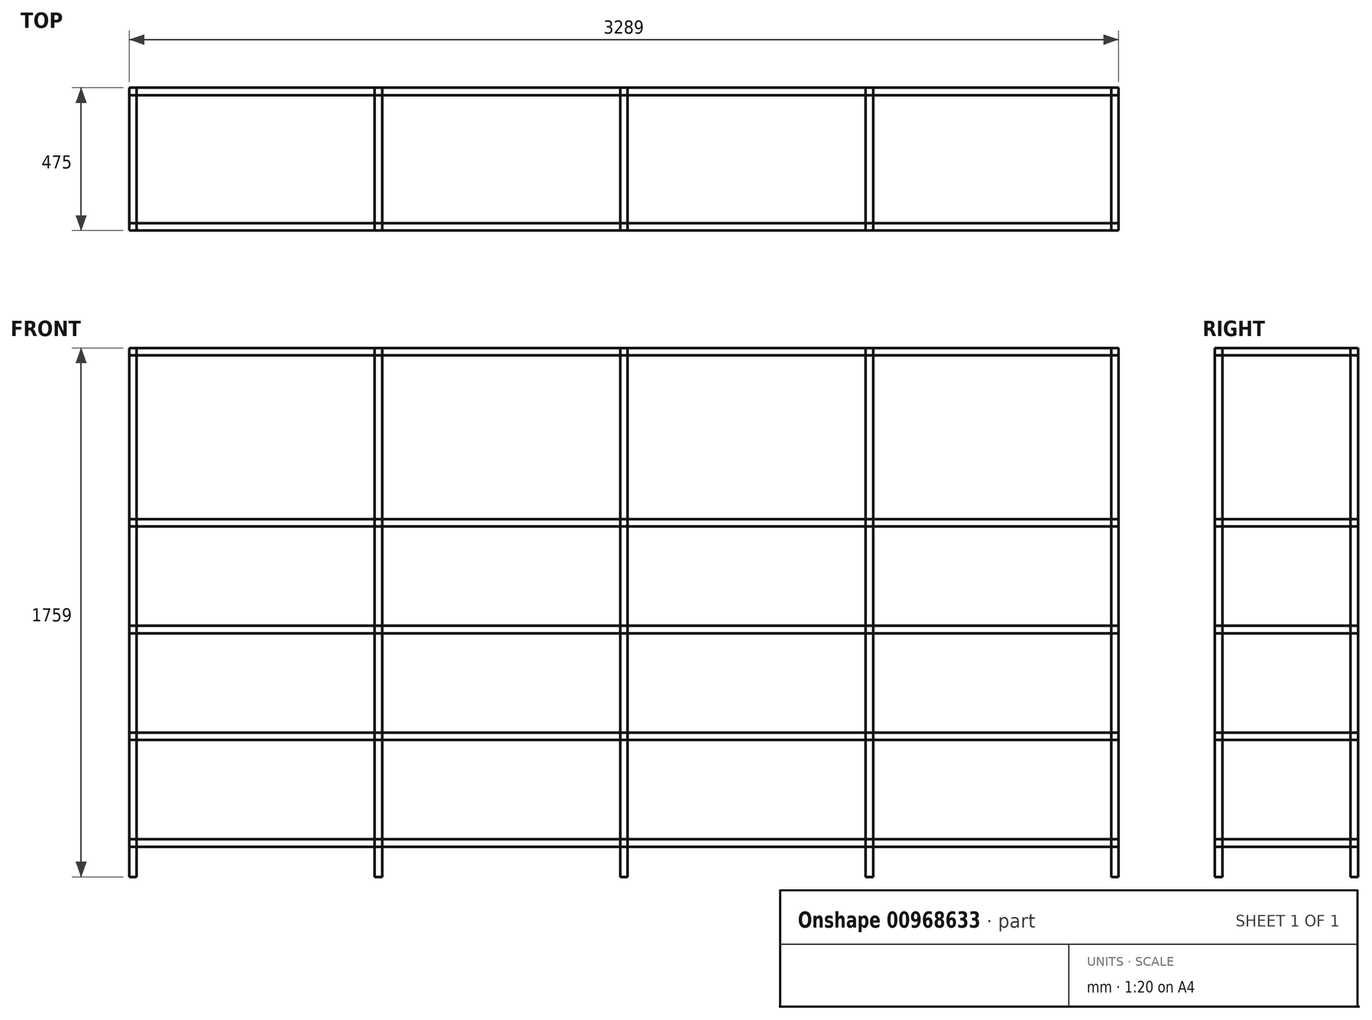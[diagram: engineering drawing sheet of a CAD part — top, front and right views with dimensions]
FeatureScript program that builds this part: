
annotation { "Feature Type Name" : "Feature", "Feature Type Description" : "" }
export const myFeature = defineFeature(function(context is Context, id is Id, definition is map)
    precondition{}
    {
        {
            var Q0;
            Q0=qCreatedBy(makeId("Top.planeOp"),FACE);
            var sketch = newSketch(context, id + "F0", { "sketchPlane" : qUnion([Q0])});
            skLineSegment(sketch, "E0.bottom", {"start": v(-20.38, 8.23) * mm, "end": v(4.62, 8.23) * mm});
            skLineSegment(sketch, "E0.top", {"start": v(-20.38, -16.77) * mm, "end": v(4.62, -16.77) * mm});
            skLineSegment(sketch, "E0.left", {"start": v(-20.38, 8.23) * mm, "end": v(-20.38, -16.77) * mm});
            skLineSegment(sketch, "E0.right", {"start": v(4.62, 8.23) * mm, "end": v(4.62, -16.77) * mm});
            skSolve(sketch);
        }
        {
            var Q0;
            Q0 = qSketchRegion(id + "F0", true);
            extrude(context, id + "F1", {"entities" : qUnion([Q0]), "depth" : 25 * mm, "offsetDistance" : 25 * mm});
        }
        {
            var Q0;
            Q0=makeQuery(id+"F1.opExtrude","SWEPT_FACE",FACE,{"disambiguationData":[OSD([sQuery(id+"F0.wireOp",EDGE,"E0.right")])]});
            extrude(context, id + "F2", {"entities" : qUnion([Q0]), "depth" : 791 * mm, "offsetDistance" : 25 * mm, "hasSecondDirection" : true, "secondDirectionOppositeDirection" : true, "secondDirectionDepth" : 0 * mm});
        }
        {
            var Q0;
            Q0=makeQuery(id+"F2.opExtrude","CAP_FACE",FACE,{"disambiguationData":[OSD([sQuery(id+"F0.wireOp",EDGE,"E0.right")])],"isStart":false});
            extrude(context, id + "F3", {"entities" : qUnion([Q0]), "depth" : 25 * mm, "offsetDistance" : 25 * mm, "hasSecondDirection" : true, "secondDirectionOppositeDirection" : true, "secondDirectionDepth" : 0 * mm});
        }
        {
            var Q0;
            Q0=makeQuery(id+"F3.opExtrude","SWEPT_FACE",FACE,{"disambiguationData":[OSD([sQuery(id+"F0.wireOp",EDGE,"E0.top"),sQuery(id+"F0.wireOp",EDGE,"E0.right")])]});
            var Q1;
            Q1=makeQuery(id+"F1.opExtrude","SWEPT_FACE",FACE,{"disambiguationData":[OSD([sQuery(id+"F0.wireOp",EDGE,"E0.top")])]});
            extrude(context, id + "F4", {"entities" : qUnion([Q0, Q1]), "depth" : 425 * mm, "offsetDistance" : 25 * mm, "hasSecondDirection" : true, "secondDirectionOppositeDirection" : true, "secondDirectionDepth" : 0 * mm});
        }
        {
            var Q0;
            Q0=makeQuery(id+"F4.opExtrude","CAP_FACE",FACE,{"disambiguationData":[OSD([sQuery(id+"F0.wireOp",EDGE,"E0.top")])],"isStart":false});
            var Q1;
            Q1=makeQuery(id+"F4.opExtrude","CAP_FACE",FACE,{"disambiguationData":[OSD([sQuery(id+"F0.wireOp",EDGE,"E0.top"),sQuery(id+"F0.wireOp",EDGE,"E0.right")])],"isStart":false});
            extrude(context, id + "F5", {"entities" : qUnion([Q0, Q1]), "depth" : 25 * mm, "offsetDistance" : 25 * mm, "hasSecondDirection" : true, "secondDirectionOppositeDirection" : true, "secondDirectionDepth" : 0 * mm});
        }
        {
            var Q0;
            {var subQ0=sQuery(id+"F0.wireOp",EDGE,"E0.right");var subQ1=sQuery(id+"F0.wireOp",EDGE,"E0.top");Q0=makeQuery(id+"F5.opExtrude","SWEPT_FACE",FACE,{"disambiguationData":[OSD([subQ1,subQ0]),TDD([makeQuery(id+"F4.opExtrude","CAP_EDGE",EDGE,{"disambiguationData":[OSD([subQ1,subQ0]),TDD([makeQuery(id+"F1.opExtrude","SWEPT_EDGE",EDGE,{"disambiguationData":[OSD([subQ1,subQ0])]})])],"isStart":false})])]});}
            extrude(context, id + "F6", {"entities" : qUnion([Q0]), "depth" : 791 * mm, "offsetDistance" : 25 * mm, "hasSecondDirection" : true, "secondDirectionOppositeDirection" : true, "secondDirectionDepth" : 0 * mm});
        }
        {
            var Q0;
            {var subQ0=sQuery(id+"F0.wireOp",EDGE,"E0.top");Q0=makeQuery(id+"F5.opExtrude","SWEPT_FACE",FACE,{"disambiguationData":[OSD([subQ0]),TDD([makeQuery(id+"F4.opExtrude","CAP_EDGE",EDGE,{"disambiguationData":[OSD([subQ0]),TDD([makeQuery(id+"F1.opExtrude","CAP_EDGE",EDGE,{"disambiguationData":[OSD([subQ0])],"isStart":false})])],"isStart":false})])]});}
            var Q1;
            Q1=makeQuery(id+"F1.opExtrude","CAP_FACE",FACE,{"disambiguationData":[OSD([sQuery(id+"F0.wireOp",EDGE,"E0.bottom"),sQuery(id+"F0.wireOp",EDGE,"E0.top"),sQuery(id+"F0.wireOp",EDGE,"E0.left"),sQuery(id+"F0.wireOp",EDGE,"E0.right")])],"isStart":false});
            var Q2;
            {var subQ0=sQuery(id+"F0.wireOp",EDGE,"E0.right");Q2=makeQuery(id+"F3.opExtrude","SWEPT_FACE",FACE,{"disambiguationData":[OSD([subQ0]),TDD([makeQuery(id+"F2.opExtrude","CAP_EDGE",EDGE,{"disambiguationData":[OSD([subQ0]),TDD([makeQuery(id+"F1.opExtrude","CAP_EDGE",EDGE,{"disambiguationData":[OSD([subQ0])],"isStart":false})])],"isStart":false})])]});}
            var Q3;
            {var subQ0=sQuery(id+"F0.wireOp",EDGE,"E0.right");var subQ1=sQuery(id+"F0.wireOp",EDGE,"E0.top");Q3=makeQuery(id+"F5.opExtrude","SWEPT_FACE",FACE,{"disambiguationData":[OSD([subQ1,subQ0]),TDD([makeQuery(id+"F4.opExtrude","CAP_EDGE",EDGE,{"disambiguationData":[OSD([subQ1,subQ0]),TDD([makeQuery(id+"F3.opExtrude","SWEPT_EDGE",EDGE,{"disambiguationData":[OSD([subQ1,subQ0]),TDD([makeQuery(id+"F2.opExtrude","CAP_VERTEX",VERTEX,{"disambiguationData":[OSD([subQ1,subQ0]),TDD([makeQuery(id+"F1.opExtrude","CAP_VERTEX",VERTEX,{"disambiguationData":[OSD([subQ1,subQ0])],"isStart":false})])],"isStart":false})])]})])],"isStart":false})])]});}
            extrude(context, id + "F7", {"entities" : qUnion([Q0, Q1, Q2, Q3]), "depth" : 544 * mm, "offsetDistance" : 25 * mm, "hasSecondDirection" : true, "secondDirectionOppositeDirection" : true, "secondDirectionDepth" : 0 * mm});
        }
        {
            var Q0;
            Q0=makeQuery(id+"F7.opExtrude","CAP_FACE",FACE,{"disambiguationData":[OSD([sQuery(id+"F0.wireOp",EDGE,"E0.bottom"),sQuery(id+"F0.wireOp",EDGE,"E0.top"),sQuery(id+"F0.wireOp",EDGE,"E0.left"),sQuery(id+"F0.wireOp",EDGE,"E0.right")])],"isStart":false});
            var Q1;
            Q1=makeQuery(id+"F7.opExtrude","CAP_FACE",FACE,{"disambiguationData":[OSD([sQuery(id+"F0.wireOp",EDGE,"E0.top")])],"isStart":false});
            var Q2;
            Q2=makeQuery(id+"F7.opExtrude","CAP_FACE",FACE,{"disambiguationData":[OSD([sQuery(id+"F0.wireOp",EDGE,"E0.top"),sQuery(id+"F0.wireOp",EDGE,"E0.right")])],"isStart":false});
            var Q3;
            Q3=makeQuery(id+"F7.opExtrude","CAP_FACE",FACE,{"disambiguationData":[OSD([sQuery(id+"F0.wireOp",EDGE,"E0.right")])],"isStart":false});
            extrude(context, id + "F8", {"entities" : qUnion([Q0, Q1, Q2, Q3]), "depth" : 25 * mm, "offsetDistance" : 25 * mm, "hasSecondDirection" : true, "secondDirectionOppositeDirection" : true, "secondDirectionDepth" : 0 * mm});
        }
        {
            var Q0;
            {var subQ0=sQuery(id+"F0.wireOp",EDGE,"E0.right");Q0=makeQuery(id+"F8.opExtrude","SWEPT_FACE",FACE,{"disambiguationData":[OSD([subQ0]),TDD([makeQuery(id+"F7.opExtrude","CAP_EDGE",EDGE,{"disambiguationData":[OSD([subQ0]),TDD([makeQuery(id+"F1.opExtrude","CAP_EDGE",EDGE,{"disambiguationData":[OSD([subQ0])],"isStart":false})])],"isStart":false})])]});}
            var Q1;
            {var subQ0=sQuery(id+"F0.wireOp",EDGE,"E0.right");var subQ1=sQuery(id+"F0.wireOp",EDGE,"E0.top");Q1=makeQuery(id+"F8.opExtrude","SWEPT_FACE",FACE,{"disambiguationData":[OSD([subQ1,subQ0]),TDD([makeQuery(id+"F7.opExtrude","CAP_EDGE",EDGE,{"disambiguationData":[OSD([subQ1,subQ0]),TDD([makeQuery(id+"F5.opExtrude","SWEPT_EDGE",EDGE,{"disambiguationData":[OSD([subQ1,subQ0]),TDD([makeQuery(id+"F4.opExtrude","CAP_VERTEX",VERTEX,{"disambiguationData":[OSD([subQ1,subQ0]),TDD([makeQuery(id+"F1.opExtrude","CAP_VERTEX",VERTEX,{"disambiguationData":[OSD([subQ1,subQ0])],"isStart":false})])],"isStart":false})])]})])],"isStart":false})])]});}
            extrude(context, id + "F9", {"entities" : qUnion([Q0, Q1]), "depth" : 791 * mm, "offsetDistance" : 25 * mm, "hasSecondDirection" : true, "secondDirectionOppositeDirection" : true, "secondDirectionDepth" : 0 * mm});
        }
        {
            var Q0;
            {var subQ0=sQuery(id+"F0.wireOp",EDGE,"E0.right");var subQ1=sQuery(id+"F0.wireOp",EDGE,"E0.top");Q0=makeQuery(id+"F8.opExtrude","SWEPT_FACE",FACE,{"disambiguationData":[OSD([subQ1,subQ0]),TDD([makeQuery(id+"F7.opExtrude","CAP_EDGE",EDGE,{"disambiguationData":[OSD([subQ1,subQ0]),TDD([makeQuery(id+"F5.opExtrude","CAP_EDGE",EDGE,{"disambiguationData":[OSD([subQ1,subQ0]),TDD([makeQuery(id+"F4.opExtrude","CAP_EDGE",EDGE,{"disambiguationData":[OSD([subQ1,subQ0]),TDD([makeQuery(id+"F3.opExtrude","SWEPT_EDGE",EDGE,{"disambiguationData":[OSD([subQ1,subQ0]),TDD([makeQuery(id+"F2.opExtrude","CAP_VERTEX",VERTEX,{"disambiguationData":[OSD([subQ1,subQ0]),TDD([makeQuery(id+"F1.opExtrude","CAP_VERTEX",VERTEX,{"disambiguationData":[OSD([subQ1,subQ0])],"isStart":false})])],"isStart":false})])]})])],"isStart":false})])],"isStart":true})])],"isStart":false})])]});}
            extrude(context, id + "F10", {"entities" : qUnion([Q0]), "depth" : 425 * mm, "offsetDistance" : 25 * mm});
        }
        {
            var Q0;
            {var subQ0=sQuery(id+"F0.wireOp",EDGE,"E0.top");Q0=makeQuery(id+"F8.opExtrude","SWEPT_FACE",FACE,{"disambiguationData":[OSD([subQ0]),TDD([makeQuery(id+"F7.opExtrude","CAP_EDGE",EDGE,{"disambiguationData":[OSD([subQ0]),TDD([makeQuery(id+"F5.opExtrude","CAP_EDGE",EDGE,{"disambiguationData":[OSD([subQ0]),TDD([makeQuery(id+"F4.opExtrude","CAP_EDGE",EDGE,{"disambiguationData":[OSD([subQ0]),TDD([makeQuery(id+"F1.opExtrude","CAP_EDGE",EDGE,{"disambiguationData":[OSD([subQ0])],"isStart":false})])],"isStart":false})])],"isStart":true})])],"isStart":false})])]});}
            extrude(context, id + "F11", {"entities" : qUnion([Q0]), "depth" : 425 * mm, "offsetDistance" : 25 * mm, "hasSecondDirection" : true, "secondDirectionOppositeDirection" : true, "secondDirectionDepth" : 0 * mm});
        }
        {
            var Q0;
            {var subQ0=sQuery(id+"F0.wireOp",EDGE,"E0.right");var subQ1=sQuery(id+"F0.wireOp",EDGE,"E0.top");Q0=makeQuery(id+"F5.opExtrude","SWEPT_FACE",FACE,{"disambiguationData":[OSD([subQ1,subQ0]),TDD([makeQuery(id+"F4.opExtrude","CAP_EDGE",EDGE,{"disambiguationData":[OSD([subQ1,subQ0]),TDD([makeQuery(id+"F3.opExtrude","SWEPT_EDGE",EDGE,{"disambiguationData":[OSD([subQ1,subQ0]),TDD([makeQuery(id+"F2.opExtrude","CAP_VERTEX",VERTEX,{"disambiguationData":[OSD([subQ1,subQ0]),TDD([makeQuery(id+"F1.opExtrude","CAP_VERTEX",VERTEX,{"disambiguationData":[OSD([subQ1,subQ0])],"isStart":true})])],"isStart":false})])]})])],"isStart":false})])]});}
            var Q1;
            {var subQ0=sQuery(id+"F0.wireOp",EDGE,"E0.right");Q1=makeQuery(id+"F3.opExtrude","SWEPT_FACE",FACE,{"disambiguationData":[OSD([subQ0]),TDD([makeQuery(id+"F2.opExtrude","CAP_EDGE",EDGE,{"disambiguationData":[OSD([subQ0]),TDD([makeQuery(id+"F1.opExtrude","CAP_EDGE",EDGE,{"disambiguationData":[OSD([subQ0])],"isStart":true})])],"isStart":false})])]});}
            var Q2;
            {var subQ0=sQuery(id+"F0.wireOp",EDGE,"E0.top");Q2=makeQuery(id+"F5.opExtrude","SWEPT_FACE",FACE,{"disambiguationData":[OSD([subQ0]),TDD([makeQuery(id+"F4.opExtrude","CAP_EDGE",EDGE,{"disambiguationData":[OSD([subQ0]),TDD([makeQuery(id+"F1.opExtrude","CAP_EDGE",EDGE,{"disambiguationData":[OSD([subQ0])],"isStart":true})])],"isStart":false})])]});}
            var Q3;
            Q3=makeQuery(id+"F1.opExtrude","CAP_FACE",FACE,{"disambiguationData":[OSD([sQuery(id+"F0.wireOp",EDGE,"E0.bottom"),sQuery(id+"F0.wireOp",EDGE,"E0.top"),sQuery(id+"F0.wireOp",EDGE,"E0.left"),sQuery(id+"F0.wireOp",EDGE,"E0.right")])],"isStart":true});
            extrude(context, id + "F12", {"entities" : qUnion([Q0, Q1, Q2, Q3]), "depth" : 330 * mm, "offsetDistance" : 25 * mm, "hasSecondDirection" : true, "secondDirectionOppositeDirection" : true, "secondDirectionDepth" : 0 * mm});
        }
        {
            var Q0;
            Q0=makeQuery(id+"F12.opExtrude","CAP_FACE",FACE,{"disambiguationData":[OSD([sQuery(id+"F0.wireOp",EDGE,"E0.top")])],"isStart":false});
            extrude(context, id + "F13", {"entities" : qUnion([Q0]), "depth" : 25 * mm, "offsetDistance" : 25 * mm, "hasSecondDirection" : true, "secondDirectionOppositeDirection" : true, "secondDirectionDepth" : 0 * mm});
        }
        {
            var Q0;
            Q0=makeQuery(id+"F13.opExtrude","CAP_FACE",FACE,{"disambiguationData":[OSD([sQuery(id+"F0.wireOp",EDGE,"E0.top")])],"isStart":false});
            extrude(context, id + "F14", {"entities" : qUnion([Q0]), "depth" : 330 * mm, "offsetDistance" : 25 * mm, "hasSecondDirection" : true, "secondDirectionOppositeDirection" : true, "secondDirectionDepth" : 0 * mm});
        }
        {
            var Q0;
            Q0=makeQuery(id+"F14.opExtrude","CAP_FACE",FACE,{"disambiguationData":[OSD([sQuery(id+"F0.wireOp",EDGE,"E0.top")])],"isStart":false});
            extrude(context, id + "F15", {"entities" : qUnion([Q0]), "depth" : 25 * mm, "offsetDistance" : 25 * mm, "hasSecondDirection" : true, "secondDirectionOppositeDirection" : true, "secondDirectionDepth" : 0 * mm});
        }
        {
            var Q0;
            Q0=makeQuery(id+"F15.opExtrude","CAP_FACE",FACE,{"disambiguationData":[OSD([sQuery(id+"F0.wireOp",EDGE,"E0.top")])],"isStart":false});
            extrude(context, id + "F16", {"entities" : qUnion([Q0]), "depth" : 330 * mm, "offsetDistance" : 25 * mm, "hasSecondDirection" : true, "secondDirectionOppositeDirection" : true, "secondDirectionDepth" : 0 * mm});
        }
        {
            var Q0;
            Q0=makeQuery(id+"F16.opExtrude","CAP_FACE",FACE,{"disambiguationData":[OSD([sQuery(id+"F0.wireOp",EDGE,"E0.top")])],"isStart":false});
            extrude(context, id + "F17", {"entities" : qUnion([Q0]), "depth" : 25 * mm, "offsetDistance" : 25 * mm, "hasSecondDirection" : true, "secondDirectionOppositeDirection" : true, "secondDirectionDepth" : 0 * mm});
        }
        {
            var Q0;
            Q0=makeQuery(id+"F17.opExtrude","CAP_FACE",FACE,{"disambiguationData":[OSD([sQuery(id+"F0.wireOp",EDGE,"E0.top")])],"isStart":false});
            extrude(context, id + "F18", {"entities" : qUnion([Q0]), "depth" : 100 * mm, "offsetDistance" : 25 * mm, "hasSecondDirection" : true, "secondDirectionOppositeDirection" : true, "secondDirectionDepth" : 0 * mm});
        }
        {
            var Q0;
            Q0=makeQuery(id+"F12.opExtrude","SWEPT_BODY",BODY,{"disambiguationData":[OSD([sQuery(id+"F0.wireOp",EDGE,"E0.bottom"),sQuery(id+"F0.wireOp",EDGE,"E0.top"),sQuery(id+"F0.wireOp",EDGE,"E0.left"),sQuery(id+"F0.wireOp",EDGE,"E0.right")])]});
            deleteBodies(context, id + "F19", {"entities" : qUnion([Q0])});
        }
        {
            var Q0;
            Q0=makeQuery(id+"F12.opExtrude","SWEPT_BODY",BODY,{"disambiguationData":[OSD([sQuery(id+"F0.wireOp",EDGE,"E0.top"),sQuery(id+"F0.wireOp",EDGE,"E0.right")])]});
            deleteBodies(context, id + "F20", {"entities" : qUnion([Q0])});
        }
        {
            var Q0;
            Q0=makeQuery(id+"F12.opExtrude","SWEPT_BODY",BODY,{"disambiguationData":[OSD([sQuery(id+"F0.wireOp",EDGE,"E0.right")])]});
            deleteBodies(context, id + "F21", {"entities" : qUnion([Q0])});
        }
        {
            var Q0;
            Q0=makeQuery(id+"F12.opExtrude","SWEPT_BODY",BODY,{"disambiguationData":[OSD([sQuery(id+"F0.wireOp",EDGE,"E0.top")])]});
            var Q1;
            Q1=makeQuery(id+"F13.opExtrude","SWEPT_BODY",BODY,{"disambiguationData":[OSD([sQuery(id+"F0.wireOp",EDGE,"E0.top")])]});
            var Q2;
            Q2=makeQuery(id+"F14.opExtrude","SWEPT_BODY",BODY,{"disambiguationData":[OSD([sQuery(id+"F0.wireOp",EDGE,"E0.top")])]});
            var Q3;
            Q3=makeQuery(id+"F15.opExtrude","SWEPT_BODY",BODY,{"disambiguationData":[OSD([sQuery(id+"F0.wireOp",EDGE,"E0.top")])]});
            var Q4;
            Q4=makeQuery(id+"F16.opExtrude","SWEPT_BODY",BODY,{"disambiguationData":[OSD([sQuery(id+"F0.wireOp",EDGE,"E0.top")])]});
            var Q5;
            Q5=makeQuery(id+"F17.opExtrude","SWEPT_BODY",BODY,{"disambiguationData":[OSD([sQuery(id+"F0.wireOp",EDGE,"E0.top")])]});
            var Q6;
            Q6=makeQuery(id+"F18.opExtrude","SWEPT_BODY",BODY,{"disambiguationData":[OSD([sQuery(id+"F0.wireOp",EDGE,"E0.top")])]});
            transform(context, id + "F22", {"entities" : qUnion([Q0, Q1, Q2, Q3, Q4, Q5, Q6]), "transformType" : TransformType.TRANSLATION_3D, "dx" : 816 * mm, "dy" : 0 * mm, "dz" : 0 * mm, "makeCopy" : true});
        }
        {
            var Q0;
            Q0=makeQuery(id+"F22.opPattern","COPY",BODY,{"derivedFrom":makeQuery(id+"F12.opExtrude","SWEPT_BODY",BODY,{"disambiguationData":[OSD([sQuery(id+"F0.wireOp",EDGE,"E0.top")])]}),"instanceName":"1"});
            var Q1;
            Q1=makeQuery(id+"F22.opPattern","COPY",BODY,{"derivedFrom":makeQuery(id+"F13.opExtrude","SWEPT_BODY",BODY,{"disambiguationData":[OSD([sQuery(id+"F0.wireOp",EDGE,"E0.top")])]}),"instanceName":"1"});
            var Q2;
            Q2=makeQuery(id+"F22.opPattern","COPY",BODY,{"derivedFrom":makeQuery(id+"F14.opExtrude","SWEPT_BODY",BODY,{"disambiguationData":[OSD([sQuery(id+"F0.wireOp",EDGE,"E0.top")])]}),"instanceName":"1"});
            var Q3;
            Q3=makeQuery(id+"F22.opPattern","COPY",BODY,{"derivedFrom":makeQuery(id+"F18.opExtrude","SWEPT_BODY",BODY,{"disambiguationData":[OSD([sQuery(id+"F0.wireOp",EDGE,"E0.top")])]}),"instanceName":"1"});
            var Q4;
            Q4=makeQuery(id+"F22.opPattern","COPY",BODY,{"derivedFrom":makeQuery(id+"F16.opExtrude","SWEPT_BODY",BODY,{"disambiguationData":[OSD([sQuery(id+"F0.wireOp",EDGE,"E0.top")])]}),"instanceName":"1"});
            var Q5;
            Q5=makeQuery(id+"F22.opPattern","COPY",BODY,{"derivedFrom":makeQuery(id+"F17.opExtrude","SWEPT_BODY",BODY,{"disambiguationData":[OSD([sQuery(id+"F0.wireOp",EDGE,"E0.top")])]}),"instanceName":"1"});
            var Q6;
            Q6=makeQuery(id+"F22.opPattern","COPY",BODY,{"derivedFrom":makeQuery(id+"F15.opExtrude","SWEPT_BODY",BODY,{"disambiguationData":[OSD([sQuery(id+"F0.wireOp",EDGE,"E0.top")])]}),"instanceName":"1"});
            var Q7;
            Q7=makeQuery(id+"F18.opExtrude","SWEPT_BODY",BODY,{"disambiguationData":[OSD([sQuery(id+"F0.wireOp",EDGE,"E0.top")])]});
            var Q8;
            Q8=makeQuery(id+"F16.opExtrude","SWEPT_BODY",BODY,{"disambiguationData":[OSD([sQuery(id+"F0.wireOp",EDGE,"E0.top")])]});
            var Q9;
            Q9=makeQuery(id+"F12.opExtrude","SWEPT_BODY",BODY,{"disambiguationData":[OSD([sQuery(id+"F0.wireOp",EDGE,"E0.top")])]});
            var Q10;
            Q10=makeQuery(id+"F13.opExtrude","SWEPT_BODY",BODY,{"disambiguationData":[OSD([sQuery(id+"F0.wireOp",EDGE,"E0.top")])]});
            var Q11;
            Q11=makeQuery(id+"F14.opExtrude","SWEPT_BODY",BODY,{"disambiguationData":[OSD([sQuery(id+"F0.wireOp",EDGE,"E0.top")])]});
            var Q12;
            Q12=makeQuery(id+"F15.opExtrude","SWEPT_BODY",BODY,{"disambiguationData":[OSD([sQuery(id+"F0.wireOp",EDGE,"E0.top")])]});
            var Q13;
            Q13=makeQuery(id+"F17.opExtrude","SWEPT_BODY",BODY,{"disambiguationData":[OSD([sQuery(id+"F0.wireOp",EDGE,"E0.top")])]});
            transform(context, id + "F23", {"entities" : qUnion([Q0, Q1, Q2, Q3, Q4, Q5, Q6, Q7, Q8, Q9, Q10, Q11, Q12, Q13]), "transformType" : TransformType.TRANSLATION_3D, "dx" : 0 * mm, "dy" : 450 * mm, "dz" : 0 * mm, "makeCopy" : true});
        }
        {
            var Q0;
            Q0=makeQuery(id+"F6.opExtrude","SWEPT_BODY",BODY,{"disambiguationData":[OSD([sQuery(id+"F0.wireOp",EDGE,"E0.top"),sQuery(id+"F0.wireOp",EDGE,"E0.right")])]});
            var Q1;
            Q1=makeQuery(id+"F4.opExtrude","SWEPT_BODY",BODY,{"disambiguationData":[OSD([sQuery(id+"F0.wireOp",EDGE,"E0.top"),sQuery(id+"F0.wireOp",EDGE,"E0.right")])]});
            var Q2;
            Q2=makeQuery(id+"F2.opExtrude","SWEPT_BODY",BODY,{"disambiguationData":[OSD([sQuery(id+"F0.wireOp",EDGE,"E0.right")])]});
            var Q3;
            Q3=makeQuery(id+"F4.opExtrude","SWEPT_BODY",BODY,{"disambiguationData":[OSD([sQuery(id+"F0.wireOp",EDGE,"E0.top")])]});
            transform(context, id + "F24", {"entities" : qUnion([Q0, Q1, Q2, Q3]), "transformType" : TransformType.TRANSLATION_3D, "dx" : 0 * mm, "dy" : 0 * mm, "dz" : -355 * mm, "makeCopy" : true});
        }
        {
            var Q0;
            Q0=makeQuery(id+"F24.opPattern","COPY",BODY,{"derivedFrom":makeQuery(id+"F2.opExtrude","SWEPT_BODY",BODY,{"disambiguationData":[OSD([sQuery(id+"F0.wireOp",EDGE,"E0.right")])]}),"instanceName":"1"});
            var Q1;
            Q1=makeQuery(id+"F24.opPattern","COPY",BODY,{"derivedFrom":makeQuery(id+"F4.opExtrude","SWEPT_BODY",BODY,{"disambiguationData":[OSD([sQuery(id+"F0.wireOp",EDGE,"E0.top")])]}),"instanceName":"1"});
            var Q2;
            Q2=makeQuery(id+"F24.opPattern","COPY",BODY,{"derivedFrom":makeQuery(id+"F6.opExtrude","SWEPT_BODY",BODY,{"disambiguationData":[OSD([sQuery(id+"F0.wireOp",EDGE,"E0.top"),sQuery(id+"F0.wireOp",EDGE,"E0.right")])]}),"instanceName":"1"});
            var Q3;
            Q3=makeQuery(id+"F24.opPattern","COPY",BODY,{"derivedFrom":makeQuery(id+"F4.opExtrude","SWEPT_BODY",BODY,{"disambiguationData":[OSD([sQuery(id+"F0.wireOp",EDGE,"E0.top"),sQuery(id+"F0.wireOp",EDGE,"E0.right")])]}),"instanceName":"1"});
            transform(context, id + "F25", {"entities" : qUnion([Q0, Q1, Q2, Q3]), "transformType" : TransformType.TRANSLATION_3D, "dx" : 0 * mm, "dy" : 0 * mm, "dz" : -355 * mm, "makeCopy" : true});
        }
        {
            var Q0;
            Q0=makeQuery(id+"F25.opPattern","COPY",BODY,{"derivedFrom":makeQuery(id+"F24.opPattern","COPY",BODY,{"derivedFrom":makeQuery(id+"F2.opExtrude","SWEPT_BODY",BODY,{"disambiguationData":[OSD([sQuery(id+"F0.wireOp",EDGE,"E0.right")])]}),"instanceName":"1"}),"instanceName":"1"});
            var Q1;
            Q1=makeQuery(id+"F25.opPattern","COPY",BODY,{"derivedFrom":makeQuery(id+"F24.opPattern","COPY",BODY,{"derivedFrom":makeQuery(id+"F4.opExtrude","SWEPT_BODY",BODY,{"disambiguationData":[OSD([sQuery(id+"F0.wireOp",EDGE,"E0.top")])]}),"instanceName":"1"}),"instanceName":"1"});
            var Q2;
            Q2=makeQuery(id+"F25.opPattern","COPY",BODY,{"derivedFrom":makeQuery(id+"F24.opPattern","COPY",BODY,{"derivedFrom":makeQuery(id+"F6.opExtrude","SWEPT_BODY",BODY,{"disambiguationData":[OSD([sQuery(id+"F0.wireOp",EDGE,"E0.top"),sQuery(id+"F0.wireOp",EDGE,"E0.right")])]}),"instanceName":"1"}),"instanceName":"1"});
            var Q3;
            Q3=makeQuery(id+"F25.opPattern","COPY",BODY,{"derivedFrom":makeQuery(id+"F24.opPattern","COPY",BODY,{"derivedFrom":makeQuery(id+"F4.opExtrude","SWEPT_BODY",BODY,{"disambiguationData":[OSD([sQuery(id+"F0.wireOp",EDGE,"E0.top"),sQuery(id+"F0.wireOp",EDGE,"E0.right")])]}),"instanceName":"1"}),"instanceName":"1"});
            transform(context, id + "F26", {"entities" : qUnion([Q0, Q1, Q2, Q3]), "transformType" : TransformType.TRANSLATION_3D, "dx" : 0 * mm, "dy" : 0 * mm, "dz" : -355 * mm, "makeCopy" : true});
        }
        {
            var Q0;
            Q0=makeQuery(id+"F9.opExtrude","SWEPT_BODY",BODY,{"disambiguationData":[OSD([sQuery(id+"F0.wireOp",EDGE,"E0.right")])]});
            var Q1;
            Q1=makeQuery(id+"F9.opExtrude","SWEPT_BODY",BODY,{"disambiguationData":[OSD([sQuery(id+"F0.wireOp",EDGE,"E0.top"),sQuery(id+"F0.wireOp",EDGE,"E0.right")])]});
            var Q2;
            Q2=makeQuery(id+"F6.opExtrude","SWEPT_BODY",BODY,{"disambiguationData":[OSD([sQuery(id+"F0.wireOp",EDGE,"E0.top"),sQuery(id+"F0.wireOp",EDGE,"E0.right")])]});
            var Q3;
            Q3=makeQuery(id+"F2.opExtrude","SWEPT_BODY",BODY,{"disambiguationData":[OSD([sQuery(id+"F0.wireOp",EDGE,"E0.right")])]});
            var Q4;
            Q4=makeQuery(id+"F24.opPattern","COPY",BODY,{"derivedFrom":makeQuery(id+"F2.opExtrude","SWEPT_BODY",BODY,{"disambiguationData":[OSD([sQuery(id+"F0.wireOp",EDGE,"E0.right")])]}),"instanceName":"1"});
            var Q5;
            Q5=makeQuery(id+"F24.opPattern","COPY",BODY,{"derivedFrom":makeQuery(id+"F6.opExtrude","SWEPT_BODY",BODY,{"disambiguationData":[OSD([sQuery(id+"F0.wireOp",EDGE,"E0.top"),sQuery(id+"F0.wireOp",EDGE,"E0.right")])]}),"instanceName":"1"});
            var Q6;
            Q6=makeQuery(id+"F25.opPattern","COPY",BODY,{"derivedFrom":makeQuery(id+"F24.opPattern","COPY",BODY,{"derivedFrom":makeQuery(id+"F6.opExtrude","SWEPT_BODY",BODY,{"disambiguationData":[OSD([sQuery(id+"F0.wireOp",EDGE,"E0.top"),sQuery(id+"F0.wireOp",EDGE,"E0.right")])]}),"instanceName":"1"}),"instanceName":"1"});
            var Q7;
            Q7=makeQuery(id+"F25.opPattern","COPY",BODY,{"derivedFrom":makeQuery(id+"F24.opPattern","COPY",BODY,{"derivedFrom":makeQuery(id+"F2.opExtrude","SWEPT_BODY",BODY,{"disambiguationData":[OSD([sQuery(id+"F0.wireOp",EDGE,"E0.right")])]}),"instanceName":"1"}),"instanceName":"1"});
            var Q8;
            Q8=makeQuery(id+"F26.opPattern","COPY",BODY,{"derivedFrom":makeQuery(id+"F25.opPattern","COPY",BODY,{"derivedFrom":makeQuery(id+"F24.opPattern","COPY",BODY,{"derivedFrom":makeQuery(id+"F6.opExtrude","SWEPT_BODY",BODY,{"disambiguationData":[OSD([sQuery(id+"F0.wireOp",EDGE,"E0.top"),sQuery(id+"F0.wireOp",EDGE,"E0.right")])]}),"instanceName":"1"}),"instanceName":"1"}),"instanceName":"1"});
            var Q9;
            Q9=makeQuery(id+"F10.opExtrude","SWEPT_BODY",BODY,{"disambiguationData":[OSD([sQuery(id+"F0.wireOp",EDGE,"E0.top"),sQuery(id+"F0.wireOp",EDGE,"E0.right")])]});
            var Q10;
            Q10=makeQuery(id+"F4.opExtrude","SWEPT_BODY",BODY,{"disambiguationData":[OSD([sQuery(id+"F0.wireOp",EDGE,"E0.top"),sQuery(id+"F0.wireOp",EDGE,"E0.right")])]});
            var Q11;
            Q11=makeQuery(id+"F24.opPattern","COPY",BODY,{"derivedFrom":makeQuery(id+"F4.opExtrude","SWEPT_BODY",BODY,{"disambiguationData":[OSD([sQuery(id+"F0.wireOp",EDGE,"E0.top"),sQuery(id+"F0.wireOp",EDGE,"E0.right")])]}),"instanceName":"1"});
            var Q12;
            Q12=makeQuery(id+"F25.opPattern","COPY",BODY,{"derivedFrom":makeQuery(id+"F24.opPattern","COPY",BODY,{"derivedFrom":makeQuery(id+"F4.opExtrude","SWEPT_BODY",BODY,{"disambiguationData":[OSD([sQuery(id+"F0.wireOp",EDGE,"E0.top"),sQuery(id+"F0.wireOp",EDGE,"E0.right")])]}),"instanceName":"1"}),"instanceName":"1"});
            var Q13;
            Q13=makeQuery(id+"F26.opPattern","COPY",BODY,{"derivedFrom":makeQuery(id+"F25.opPattern","COPY",BODY,{"derivedFrom":makeQuery(id+"F24.opPattern","COPY",BODY,{"derivedFrom":makeQuery(id+"F4.opExtrude","SWEPT_BODY",BODY,{"disambiguationData":[OSD([sQuery(id+"F0.wireOp",EDGE,"E0.top"),sQuery(id+"F0.wireOp",EDGE,"E0.right")])]}),"instanceName":"1"}),"instanceName":"1"}),"instanceName":"1"});
            var Q14;
            Q14=makeQuery(id+"F26.opPattern","COPY",BODY,{"derivedFrom":makeQuery(id+"F25.opPattern","COPY",BODY,{"derivedFrom":makeQuery(id+"F24.opPattern","COPY",BODY,{"derivedFrom":makeQuery(id+"F2.opExtrude","SWEPT_BODY",BODY,{"disambiguationData":[OSD([sQuery(id+"F0.wireOp",EDGE,"E0.right")])]}),"instanceName":"1"}),"instanceName":"1"}),"instanceName":"1"});
            var Q15;
            Q15=makeQuery(id+"F7.opExtrude","SWEPT_BODY",BODY,{"disambiguationData":[OSD([sQuery(id+"F0.wireOp",EDGE,"E0.right")])]});
            var Q16;
            Q16=makeQuery(id+"F7.opExtrude","SWEPT_BODY",BODY,{"disambiguationData":[OSD([sQuery(id+"F0.wireOp",EDGE,"E0.top"),sQuery(id+"F0.wireOp",EDGE,"E0.right")])]});
            var Q17;
            Q17=makeQuery(id+"F22.opPattern","COPY",BODY,{"derivedFrom":makeQuery(id+"F12.opExtrude","SWEPT_BODY",BODY,{"disambiguationData":[OSD([sQuery(id+"F0.wireOp",EDGE,"E0.top")])]}),"instanceName":"1"});
            var Q18;
            Q18=makeQuery(id+"F23.opPattern","COPY",BODY,{"derivedFrom":makeQuery(id+"F22.opPattern","COPY",BODY,{"derivedFrom":makeQuery(id+"F12.opExtrude","SWEPT_BODY",BODY,{"disambiguationData":[OSD([sQuery(id+"F0.wireOp",EDGE,"E0.top")])]}),"instanceName":"1"}),"instanceName":"1"});
            var Q19;
            Q19=makeQuery(id+"F23.opPattern","COPY",BODY,{"derivedFrom":makeQuery(id+"F22.opPattern","COPY",BODY,{"derivedFrom":makeQuery(id+"F14.opExtrude","SWEPT_BODY",BODY,{"disambiguationData":[OSD([sQuery(id+"F0.wireOp",EDGE,"E0.top")])]}),"instanceName":"1"}),"instanceName":"1"});
            var Q20;
            Q20=makeQuery(id+"F22.opPattern","COPY",BODY,{"derivedFrom":makeQuery(id+"F14.opExtrude","SWEPT_BODY",BODY,{"disambiguationData":[OSD([sQuery(id+"F0.wireOp",EDGE,"E0.top")])]}),"instanceName":"1"});
            var Q21;
            Q21=makeQuery(id+"F23.opPattern","COPY",BODY,{"derivedFrom":makeQuery(id+"F22.opPattern","COPY",BODY,{"derivedFrom":makeQuery(id+"F16.opExtrude","SWEPT_BODY",BODY,{"disambiguationData":[OSD([sQuery(id+"F0.wireOp",EDGE,"E0.top")])]}),"instanceName":"1"}),"instanceName":"1"});
            var Q22;
            Q22=makeQuery(id+"F22.opPattern","COPY",BODY,{"derivedFrom":makeQuery(id+"F16.opExtrude","SWEPT_BODY",BODY,{"disambiguationData":[OSD([sQuery(id+"F0.wireOp",EDGE,"E0.top")])]}),"instanceName":"1"});
            var Q23;
            Q23=makeQuery(id+"F8.opExtrude","SWEPT_BODY",BODY,{"disambiguationData":[OSD([sQuery(id+"F0.wireOp",EDGE,"E0.top"),sQuery(id+"F0.wireOp",EDGE,"E0.right")])]});
            var Q24;
            Q24=makeQuery(id+"F8.opExtrude","SWEPT_BODY",BODY,{"disambiguationData":[OSD([sQuery(id+"F0.wireOp",EDGE,"E0.right")])]});
            var Q25;
            Q25=makeQuery(id+"F3.opExtrude","SWEPT_BODY",BODY,{"disambiguationData":[OSD([sQuery(id+"F0.wireOp",EDGE,"E0.right")])]});
            var Q26;
            Q26=makeQuery(id+"F23.opPattern","COPY",BODY,{"derivedFrom":makeQuery(id+"F22.opPattern","COPY",BODY,{"derivedFrom":makeQuery(id+"F13.opExtrude","SWEPT_BODY",BODY,{"disambiguationData":[OSD([sQuery(id+"F0.wireOp",EDGE,"E0.top")])]}),"instanceName":"1"}),"instanceName":"1"});
            var Q27;
            Q27=makeQuery(id+"F23.opPattern","COPY",BODY,{"derivedFrom":makeQuery(id+"F22.opPattern","COPY",BODY,{"derivedFrom":makeQuery(id+"F15.opExtrude","SWEPT_BODY",BODY,{"disambiguationData":[OSD([sQuery(id+"F0.wireOp",EDGE,"E0.top")])]}),"instanceName":"1"}),"instanceName":"1"});
            var Q28;
            Q28=makeQuery(id+"F23.opPattern","COPY",BODY,{"derivedFrom":makeQuery(id+"F22.opPattern","COPY",BODY,{"derivedFrom":makeQuery(id+"F18.opExtrude","SWEPT_BODY",BODY,{"disambiguationData":[OSD([sQuery(id+"F0.wireOp",EDGE,"E0.top")])]}),"instanceName":"1"}),"instanceName":"1"});
            var Q29;
            Q29=makeQuery(id+"F22.opPattern","COPY",BODY,{"derivedFrom":makeQuery(id+"F18.opExtrude","SWEPT_BODY",BODY,{"disambiguationData":[OSD([sQuery(id+"F0.wireOp",EDGE,"E0.top")])]}),"instanceName":"1"});
            var Q30;
            Q30=makeQuery(id+"F23.opPattern","COPY",BODY,{"derivedFrom":makeQuery(id+"F22.opPattern","COPY",BODY,{"derivedFrom":makeQuery(id+"F17.opExtrude","SWEPT_BODY",BODY,{"disambiguationData":[OSD([sQuery(id+"F0.wireOp",EDGE,"E0.top")])]}),"instanceName":"1"}),"instanceName":"1"});
            var Q31;
            Q31=makeQuery(id+"F22.opPattern","COPY",BODY,{"derivedFrom":makeQuery(id+"F15.opExtrude","SWEPT_BODY",BODY,{"disambiguationData":[OSD([sQuery(id+"F0.wireOp",EDGE,"E0.top")])]}),"instanceName":"1"});
            var Q32;
            Q32=makeQuery(id+"F22.opPattern","COPY",BODY,{"derivedFrom":makeQuery(id+"F13.opExtrude","SWEPT_BODY",BODY,{"disambiguationData":[OSD([sQuery(id+"F0.wireOp",EDGE,"E0.top")])]}),"instanceName":"1"});
            var Q33;
            Q33=makeQuery(id+"F22.opPattern","COPY",BODY,{"derivedFrom":makeQuery(id+"F17.opExtrude","SWEPT_BODY",BODY,{"disambiguationData":[OSD([sQuery(id+"F0.wireOp",EDGE,"E0.top")])]}),"instanceName":"1"});
            var Q34;
            Q34=makeQuery(id+"F5.opExtrude","SWEPT_BODY",BODY,{"disambiguationData":[OSD([sQuery(id+"F0.wireOp",EDGE,"E0.top"),sQuery(id+"F0.wireOp",EDGE,"E0.right")])]});
            transform(context, id + "F27", {"entities" : qUnion([Q0, Q1, Q2, Q3, Q4, Q5, Q6, Q7, Q8, Q9, Q10, Q11, Q12, Q13, Q14, Q15, Q16, Q17, Q18, Q19, Q20, Q21, Q22, Q23, Q24, Q25, Q26, Q27, Q28, Q29, Q30, Q31, Q32, Q33, Q34]), "transformType" : TransformType.TRANSLATION_3D, "dx" : 816 * mm, "dy" : 0 * mm, "dz" : 0 * mm, "makeCopy" : true});
        }
        {
            var Q0;
            Q0=makeQuery(id+"F9.opExtrude","SWEPT_BODY",BODY,{"disambiguationData":[OSD([sQuery(id+"F0.wireOp",EDGE,"E0.top"),sQuery(id+"F0.wireOp",EDGE,"E0.right")])]});
            var Q1;
            Q1=makeQuery(id+"F8.opExtrude","SWEPT_BODY",BODY,{"disambiguationData":[OSD([sQuery(id+"F0.wireOp",EDGE,"E0.top"),sQuery(id+"F0.wireOp",EDGE,"E0.right")])]});
            var Q2;
            Q2=makeQuery(id+"F27.opPattern","COPY",BODY,{"derivedFrom":makeQuery(id+"F9.opExtrude","SWEPT_BODY",BODY,{"disambiguationData":[OSD([sQuery(id+"F0.wireOp",EDGE,"E0.top"),sQuery(id+"F0.wireOp",EDGE,"E0.right")])]}),"instanceName":"1"});
            var Q3;
            Q3=makeQuery(id+"F27.opPattern","COPY",BODY,{"derivedFrom":makeQuery(id+"F8.opExtrude","SWEPT_BODY",BODY,{"disambiguationData":[OSD([sQuery(id+"F0.wireOp",EDGE,"E0.top"),sQuery(id+"F0.wireOp",EDGE,"E0.right")])]}),"instanceName":"1"});
            var Q4;
            Q4=makeQuery(id+"F27.opPattern","COPY",BODY,{"derivedFrom":makeQuery(id+"F7.opExtrude","SWEPT_BODY",BODY,{"disambiguationData":[OSD([sQuery(id+"F0.wireOp",EDGE,"E0.top"),sQuery(id+"F0.wireOp",EDGE,"E0.right")])]}),"instanceName":"1"});
            var Q5;
            Q5=makeQuery(id+"F27.opPattern","COPY",BODY,{"derivedFrom":makeQuery(id+"F5.opExtrude","SWEPT_BODY",BODY,{"disambiguationData":[OSD([sQuery(id+"F0.wireOp",EDGE,"E0.top"),sQuery(id+"F0.wireOp",EDGE,"E0.right")])]}),"instanceName":"1"});
            var Q6;
            Q6=makeQuery(id+"F27.opPattern","COPY",BODY,{"derivedFrom":makeQuery(id+"F22.opPattern","COPY",BODY,{"derivedFrom":makeQuery(id+"F12.opExtrude","SWEPT_BODY",BODY,{"disambiguationData":[OSD([sQuery(id+"F0.wireOp",EDGE,"E0.top")])]}),"instanceName":"1"}),"instanceName":"1"});
            var Q7;
            Q7=makeQuery(id+"F27.opPattern","COPY",BODY,{"derivedFrom":makeQuery(id+"F22.opPattern","COPY",BODY,{"derivedFrom":makeQuery(id+"F13.opExtrude","SWEPT_BODY",BODY,{"disambiguationData":[OSD([sQuery(id+"F0.wireOp",EDGE,"E0.top")])]}),"instanceName":"1"}),"instanceName":"1"});
            var Q8;
            Q8=makeQuery(id+"F27.opPattern","COPY",BODY,{"derivedFrom":makeQuery(id+"F22.opPattern","COPY",BODY,{"derivedFrom":makeQuery(id+"F14.opExtrude","SWEPT_BODY",BODY,{"disambiguationData":[OSD([sQuery(id+"F0.wireOp",EDGE,"E0.top")])]}),"instanceName":"1"}),"instanceName":"1"});
            var Q9;
            Q9=makeQuery(id+"F27.opPattern","COPY",BODY,{"derivedFrom":makeQuery(id+"F22.opPattern","COPY",BODY,{"derivedFrom":makeQuery(id+"F15.opExtrude","SWEPT_BODY",BODY,{"disambiguationData":[OSD([sQuery(id+"F0.wireOp",EDGE,"E0.top")])]}),"instanceName":"1"}),"instanceName":"1"});
            var Q10;
            Q10=makeQuery(id+"F27.opPattern","COPY",BODY,{"derivedFrom":makeQuery(id+"F22.opPattern","COPY",BODY,{"derivedFrom":makeQuery(id+"F16.opExtrude","SWEPT_BODY",BODY,{"disambiguationData":[OSD([sQuery(id+"F0.wireOp",EDGE,"E0.top")])]}),"instanceName":"1"}),"instanceName":"1"});
            var Q11;
            Q11=makeQuery(id+"F27.opPattern","COPY",BODY,{"derivedFrom":makeQuery(id+"F22.opPattern","COPY",BODY,{"derivedFrom":makeQuery(id+"F17.opExtrude","SWEPT_BODY",BODY,{"disambiguationData":[OSD([sQuery(id+"F0.wireOp",EDGE,"E0.top")])]}),"instanceName":"1"}),"instanceName":"1"});
            var Q12;
            Q12=makeQuery(id+"F27.opPattern","COPY",BODY,{"derivedFrom":makeQuery(id+"F22.opPattern","COPY",BODY,{"derivedFrom":makeQuery(id+"F18.opExtrude","SWEPT_BODY",BODY,{"disambiguationData":[OSD([sQuery(id+"F0.wireOp",EDGE,"E0.top")])]}),"instanceName":"1"}),"instanceName":"1"});
            var Q13;
            Q13=makeQuery(id+"F27.opPattern","COPY",BODY,{"derivedFrom":makeQuery(id+"F7.opExtrude","SWEPT_BODY",BODY,{"disambiguationData":[OSD([sQuery(id+"F0.wireOp",EDGE,"E0.right")])]}),"instanceName":"1"});
            var Q14;
            Q14=makeQuery(id+"F27.opPattern","COPY",BODY,{"derivedFrom":makeQuery(id+"F8.opExtrude","SWEPT_BODY",BODY,{"disambiguationData":[OSD([sQuery(id+"F0.wireOp",EDGE,"E0.right")])]}),"instanceName":"1"});
            var Q15;
            Q15=makeQuery(id+"F27.opPattern","COPY",BODY,{"derivedFrom":makeQuery(id+"F10.opExtrude","SWEPT_BODY",BODY,{"disambiguationData":[OSD([sQuery(id+"F0.wireOp",EDGE,"E0.top"),sQuery(id+"F0.wireOp",EDGE,"E0.right")])]}),"instanceName":"1"});
            var Q16;
            Q16=makeQuery(id+"F27.opPattern","COPY",BODY,{"derivedFrom":makeQuery(id+"F6.opExtrude","SWEPT_BODY",BODY,{"disambiguationData":[OSD([sQuery(id+"F0.wireOp",EDGE,"E0.top"),sQuery(id+"F0.wireOp",EDGE,"E0.right")])]}),"instanceName":"1"});
            var Q17;
            Q17=makeQuery(id+"F27.opPattern","COPY",BODY,{"derivedFrom":makeQuery(id+"F24.opPattern","COPY",BODY,{"derivedFrom":makeQuery(id+"F6.opExtrude","SWEPT_BODY",BODY,{"disambiguationData":[OSD([sQuery(id+"F0.wireOp",EDGE,"E0.top"),sQuery(id+"F0.wireOp",EDGE,"E0.right")])]}),"instanceName":"1"}),"instanceName":"1"});
            var Q18;
            Q18=makeQuery(id+"F27.opPattern","COPY",BODY,{"derivedFrom":makeQuery(id+"F25.opPattern","COPY",BODY,{"derivedFrom":makeQuery(id+"F24.opPattern","COPY",BODY,{"derivedFrom":makeQuery(id+"F6.opExtrude","SWEPT_BODY",BODY,{"disambiguationData":[OSD([sQuery(id+"F0.wireOp",EDGE,"E0.top"),sQuery(id+"F0.wireOp",EDGE,"E0.right")])]}),"instanceName":"1"}),"instanceName":"1"}),"instanceName":"1"});
            var Q19;
            Q19=makeQuery(id+"F27.opPattern","COPY",BODY,{"derivedFrom":makeQuery(id+"F26.opPattern","COPY",BODY,{"derivedFrom":makeQuery(id+"F25.opPattern","COPY",BODY,{"derivedFrom":makeQuery(id+"F24.opPattern","COPY",BODY,{"derivedFrom":makeQuery(id+"F6.opExtrude","SWEPT_BODY",BODY,{"disambiguationData":[OSD([sQuery(id+"F0.wireOp",EDGE,"E0.top"),sQuery(id+"F0.wireOp",EDGE,"E0.right")])]}),"instanceName":"1"}),"instanceName":"1"}),"instanceName":"1"}),"instanceName":"1"});
            var Q20;
            Q20=makeQuery(id+"F27.opPattern","COPY",BODY,{"derivedFrom":makeQuery(id+"F26.opPattern","COPY",BODY,{"derivedFrom":makeQuery(id+"F25.opPattern","COPY",BODY,{"derivedFrom":makeQuery(id+"F24.opPattern","COPY",BODY,{"derivedFrom":makeQuery(id+"F4.opExtrude","SWEPT_BODY",BODY,{"disambiguationData":[OSD([sQuery(id+"F0.wireOp",EDGE,"E0.top"),sQuery(id+"F0.wireOp",EDGE,"E0.right")])]}),"instanceName":"1"}),"instanceName":"1"}),"instanceName":"1"}),"instanceName":"1"});
            var Q21;
            Q21=makeQuery(id+"F27.opPattern","COPY",BODY,{"derivedFrom":makeQuery(id+"F25.opPattern","COPY",BODY,{"derivedFrom":makeQuery(id+"F24.opPattern","COPY",BODY,{"derivedFrom":makeQuery(id+"F4.opExtrude","SWEPT_BODY",BODY,{"disambiguationData":[OSD([sQuery(id+"F0.wireOp",EDGE,"E0.top"),sQuery(id+"F0.wireOp",EDGE,"E0.right")])]}),"instanceName":"1"}),"instanceName":"1"}),"instanceName":"1"});
            var Q22;
            Q22=makeQuery(id+"F27.opPattern","COPY",BODY,{"derivedFrom":makeQuery(id+"F24.opPattern","COPY",BODY,{"derivedFrom":makeQuery(id+"F4.opExtrude","SWEPT_BODY",BODY,{"disambiguationData":[OSD([sQuery(id+"F0.wireOp",EDGE,"E0.top"),sQuery(id+"F0.wireOp",EDGE,"E0.right")])]}),"instanceName":"1"}),"instanceName":"1"});
            var Q23;
            Q23=makeQuery(id+"F27.opPattern","COPY",BODY,{"derivedFrom":makeQuery(id+"F4.opExtrude","SWEPT_BODY",BODY,{"disambiguationData":[OSD([sQuery(id+"F0.wireOp",EDGE,"E0.top"),sQuery(id+"F0.wireOp",EDGE,"E0.right")])]}),"instanceName":"1"});
            var Q24;
            Q24=makeQuery(id+"F27.opPattern","COPY",BODY,{"derivedFrom":makeQuery(id+"F23.opPattern","COPY",BODY,{"derivedFrom":makeQuery(id+"F22.opPattern","COPY",BODY,{"derivedFrom":makeQuery(id+"F12.opExtrude","SWEPT_BODY",BODY,{"disambiguationData":[OSD([sQuery(id+"F0.wireOp",EDGE,"E0.top")])]}),"instanceName":"1"}),"instanceName":"1"}),"instanceName":"1"});
            var Q25;
            Q25=makeQuery(id+"F27.opPattern","COPY",BODY,{"derivedFrom":makeQuery(id+"F23.opPattern","COPY",BODY,{"derivedFrom":makeQuery(id+"F22.opPattern","COPY",BODY,{"derivedFrom":makeQuery(id+"F14.opExtrude","SWEPT_BODY",BODY,{"disambiguationData":[OSD([sQuery(id+"F0.wireOp",EDGE,"E0.top")])]}),"instanceName":"1"}),"instanceName":"1"}),"instanceName":"1"});
            var Q26;
            Q26=makeQuery(id+"F27.opPattern","COPY",BODY,{"derivedFrom":makeQuery(id+"F23.opPattern","COPY",BODY,{"derivedFrom":makeQuery(id+"F22.opPattern","COPY",BODY,{"derivedFrom":makeQuery(id+"F16.opExtrude","SWEPT_BODY",BODY,{"disambiguationData":[OSD([sQuery(id+"F0.wireOp",EDGE,"E0.top")])]}),"instanceName":"1"}),"instanceName":"1"}),"instanceName":"1"});
            var Q27;
            Q27=makeQuery(id+"F10.opExtrude","SWEPT_BODY",BODY,{"disambiguationData":[OSD([sQuery(id+"F0.wireOp",EDGE,"E0.top"),sQuery(id+"F0.wireOp",EDGE,"E0.right")])]});
            var Q28;
            Q28=makeQuery(id+"F27.opPattern","COPY",BODY,{"derivedFrom":makeQuery(id+"F9.opExtrude","SWEPT_BODY",BODY,{"disambiguationData":[OSD([sQuery(id+"F0.wireOp",EDGE,"E0.right")])]}),"instanceName":"1"});
            var Q29;
            Q29=makeQuery(id+"F9.opExtrude","SWEPT_BODY",BODY,{"disambiguationData":[OSD([sQuery(id+"F0.wireOp",EDGE,"E0.right")])]});
            var Q30;
            Q30=makeQuery(id+"F8.opExtrude","SWEPT_BODY",BODY,{"disambiguationData":[OSD([sQuery(id+"F0.wireOp",EDGE,"E0.right")])]});
            var Q31;
            Q31=makeQuery(id+"F7.opExtrude","SWEPT_BODY",BODY,{"disambiguationData":[OSD([sQuery(id+"F0.wireOp",EDGE,"E0.right")])]});
            var Q32;
            Q32=makeQuery(id+"F4.opExtrude","SWEPT_BODY",BODY,{"disambiguationData":[OSD([sQuery(id+"F0.wireOp",EDGE,"E0.top"),sQuery(id+"F0.wireOp",EDGE,"E0.right")])]});
            var Q33;
            Q33=makeQuery(id+"F24.opPattern","COPY",BODY,{"derivedFrom":makeQuery(id+"F4.opExtrude","SWEPT_BODY",BODY,{"disambiguationData":[OSD([sQuery(id+"F0.wireOp",EDGE,"E0.top"),sQuery(id+"F0.wireOp",EDGE,"E0.right")])]}),"instanceName":"1"});
            var Q34;
            Q34=makeQuery(id+"F25.opPattern","COPY",BODY,{"derivedFrom":makeQuery(id+"F24.opPattern","COPY",BODY,{"derivedFrom":makeQuery(id+"F4.opExtrude","SWEPT_BODY",BODY,{"disambiguationData":[OSD([sQuery(id+"F0.wireOp",EDGE,"E0.top"),sQuery(id+"F0.wireOp",EDGE,"E0.right")])]}),"instanceName":"1"}),"instanceName":"1"});
            var Q35;
            Q35=makeQuery(id+"F26.opPattern","COPY",BODY,{"derivedFrom":makeQuery(id+"F25.opPattern","COPY",BODY,{"derivedFrom":makeQuery(id+"F24.opPattern","COPY",BODY,{"derivedFrom":makeQuery(id+"F4.opExtrude","SWEPT_BODY",BODY,{"disambiguationData":[OSD([sQuery(id+"F0.wireOp",EDGE,"E0.top"),sQuery(id+"F0.wireOp",EDGE,"E0.right")])]}),"instanceName":"1"}),"instanceName":"1"}),"instanceName":"1"});
            var Q36;
            Q36=makeQuery(id+"F25.opPattern","COPY",BODY,{"derivedFrom":makeQuery(id+"F24.opPattern","COPY",BODY,{"derivedFrom":makeQuery(id+"F6.opExtrude","SWEPT_BODY",BODY,{"disambiguationData":[OSD([sQuery(id+"F0.wireOp",EDGE,"E0.top"),sQuery(id+"F0.wireOp",EDGE,"E0.right")])]}),"instanceName":"1"}),"instanceName":"1"});
            var Q37;
            Q37=makeQuery(id+"F24.opPattern","COPY",BODY,{"derivedFrom":makeQuery(id+"F6.opExtrude","SWEPT_BODY",BODY,{"disambiguationData":[OSD([sQuery(id+"F0.wireOp",EDGE,"E0.top"),sQuery(id+"F0.wireOp",EDGE,"E0.right")])]}),"instanceName":"1"});
            var Q38;
            Q38=makeQuery(id+"F6.opExtrude","SWEPT_BODY",BODY,{"disambiguationData":[OSD([sQuery(id+"F0.wireOp",EDGE,"E0.top"),sQuery(id+"F0.wireOp",EDGE,"E0.right")])]});
            var Q39;
            Q39=makeQuery(id+"F22.opPattern","COPY",BODY,{"derivedFrom":makeQuery(id+"F15.opExtrude","SWEPT_BODY",BODY,{"disambiguationData":[OSD([sQuery(id+"F0.wireOp",EDGE,"E0.top")])]}),"instanceName":"1"});
            var Q40;
            Q40=makeQuery(id+"F22.opPattern","COPY",BODY,{"derivedFrom":makeQuery(id+"F13.opExtrude","SWEPT_BODY",BODY,{"disambiguationData":[OSD([sQuery(id+"F0.wireOp",EDGE,"E0.top")])]}),"instanceName":"1"});
            var Q41;
            Q41=makeQuery(id+"F22.opPattern","COPY",BODY,{"derivedFrom":makeQuery(id+"F17.opExtrude","SWEPT_BODY",BODY,{"disambiguationData":[OSD([sQuery(id+"F0.wireOp",EDGE,"E0.top")])]}),"instanceName":"1"});
            var Q42;
            Q42=makeQuery(id+"F26.opPattern","COPY",BODY,{"derivedFrom":makeQuery(id+"F25.opPattern","COPY",BODY,{"derivedFrom":makeQuery(id+"F24.opPattern","COPY",BODY,{"derivedFrom":makeQuery(id+"F6.opExtrude","SWEPT_BODY",BODY,{"disambiguationData":[OSD([sQuery(id+"F0.wireOp",EDGE,"E0.top"),sQuery(id+"F0.wireOp",EDGE,"E0.right")])]}),"instanceName":"1"}),"instanceName":"1"}),"instanceName":"1"});
            var Q43;
            Q43=makeQuery(id+"F27.opPattern","COPY",BODY,{"derivedFrom":makeQuery(id+"F3.opExtrude","SWEPT_BODY",BODY,{"disambiguationData":[OSD([sQuery(id+"F0.wireOp",EDGE,"E0.right")])]}),"instanceName":"1"});
            var Q44;
            Q44=makeQuery(id+"F27.opPattern","COPY",BODY,{"derivedFrom":makeQuery(id+"F23.opPattern","COPY",BODY,{"derivedFrom":makeQuery(id+"F22.opPattern","COPY",BODY,{"derivedFrom":makeQuery(id+"F13.opExtrude","SWEPT_BODY",BODY,{"disambiguationData":[OSD([sQuery(id+"F0.wireOp",EDGE,"E0.top")])]}),"instanceName":"1"}),"instanceName":"1"}),"instanceName":"1"});
            var Q45;
            Q45=makeQuery(id+"F27.opPattern","COPY",BODY,{"derivedFrom":makeQuery(id+"F23.opPattern","COPY",BODY,{"derivedFrom":makeQuery(id+"F22.opPattern","COPY",BODY,{"derivedFrom":makeQuery(id+"F15.opExtrude","SWEPT_BODY",BODY,{"disambiguationData":[OSD([sQuery(id+"F0.wireOp",EDGE,"E0.top")])]}),"instanceName":"1"}),"instanceName":"1"}),"instanceName":"1"});
            var Q46;
            Q46=makeQuery(id+"F23.opPattern","COPY",BODY,{"derivedFrom":makeQuery(id+"F22.opPattern","COPY",BODY,{"derivedFrom":makeQuery(id+"F17.opExtrude","SWEPT_BODY",BODY,{"disambiguationData":[OSD([sQuery(id+"F0.wireOp",EDGE,"E0.top")])]}),"instanceName":"1"}),"instanceName":"1"});
            var Q47;
            Q47=makeQuery(id+"F23.opPattern","COPY",BODY,{"derivedFrom":makeQuery(id+"F22.opPattern","COPY",BODY,{"derivedFrom":makeQuery(id+"F15.opExtrude","SWEPT_BODY",BODY,{"disambiguationData":[OSD([sQuery(id+"F0.wireOp",EDGE,"E0.top")])]}),"instanceName":"1"}),"instanceName":"1"});
            var Q48;
            Q48=makeQuery(id+"F23.opPattern","COPY",BODY,{"derivedFrom":makeQuery(id+"F22.opPattern","COPY",BODY,{"derivedFrom":makeQuery(id+"F13.opExtrude","SWEPT_BODY",BODY,{"disambiguationData":[OSD([sQuery(id+"F0.wireOp",EDGE,"E0.top")])]}),"instanceName":"1"}),"instanceName":"1"});
            var Q49;
            Q49=makeQuery(id+"F3.opExtrude","SWEPT_BODY",BODY,{"disambiguationData":[OSD([sQuery(id+"F0.wireOp",EDGE,"E0.right")])]});
            var Q50;
            Q50=makeQuery(id+"F23.opPattern","COPY",BODY,{"derivedFrom":makeQuery(id+"F22.opPattern","COPY",BODY,{"derivedFrom":makeQuery(id+"F12.opExtrude","SWEPT_BODY",BODY,{"disambiguationData":[OSD([sQuery(id+"F0.wireOp",EDGE,"E0.top")])]}),"instanceName":"1"}),"instanceName":"1"});
            var Q51;
            Q51=makeQuery(id+"F27.opPattern","COPY",BODY,{"derivedFrom":makeQuery(id+"F24.opPattern","COPY",BODY,{"derivedFrom":makeQuery(id+"F2.opExtrude","SWEPT_BODY",BODY,{"disambiguationData":[OSD([sQuery(id+"F0.wireOp",EDGE,"E0.right")])]}),"instanceName":"1"}),"instanceName":"1"});
            var Q52;
            Q52=makeQuery(id+"F27.opPattern","COPY",BODY,{"derivedFrom":makeQuery(id+"F2.opExtrude","SWEPT_BODY",BODY,{"disambiguationData":[OSD([sQuery(id+"F0.wireOp",EDGE,"E0.right")])]}),"instanceName":"1"});
            var Q53;
            Q53=makeQuery(id+"F27.opPattern","COPY",BODY,{"derivedFrom":makeQuery(id+"F25.opPattern","COPY",BODY,{"derivedFrom":makeQuery(id+"F24.opPattern","COPY",BODY,{"derivedFrom":makeQuery(id+"F2.opExtrude","SWEPT_BODY",BODY,{"disambiguationData":[OSD([sQuery(id+"F0.wireOp",EDGE,"E0.right")])]}),"instanceName":"1"}),"instanceName":"1"}),"instanceName":"1"});
            var Q54;
            Q54=makeQuery(id+"F27.opPattern","COPY",BODY,{"derivedFrom":makeQuery(id+"F26.opPattern","COPY",BODY,{"derivedFrom":makeQuery(id+"F25.opPattern","COPY",BODY,{"derivedFrom":makeQuery(id+"F24.opPattern","COPY",BODY,{"derivedFrom":makeQuery(id+"F2.opExtrude","SWEPT_BODY",BODY,{"disambiguationData":[OSD([sQuery(id+"F0.wireOp",EDGE,"E0.right")])]}),"instanceName":"1"}),"instanceName":"1"}),"instanceName":"1"}),"instanceName":"1"});
            var Q55;
            Q55=makeQuery(id+"F23.opPattern","COPY",BODY,{"derivedFrom":makeQuery(id+"F22.opPattern","COPY",BODY,{"derivedFrom":makeQuery(id+"F16.opExtrude","SWEPT_BODY",BODY,{"disambiguationData":[OSD([sQuery(id+"F0.wireOp",EDGE,"E0.top")])]}),"instanceName":"1"}),"instanceName":"1"});
            var Q56;
            Q56=makeQuery(id+"F23.opPattern","COPY",BODY,{"derivedFrom":makeQuery(id+"F22.opPattern","COPY",BODY,{"derivedFrom":makeQuery(id+"F14.opExtrude","SWEPT_BODY",BODY,{"disambiguationData":[OSD([sQuery(id+"F0.wireOp",EDGE,"E0.top")])]}),"instanceName":"1"}),"instanceName":"1"});
            var Q57;
            Q57=makeQuery(id+"F24.opPattern","COPY",BODY,{"derivedFrom":makeQuery(id+"F2.opExtrude","SWEPT_BODY",BODY,{"disambiguationData":[OSD([sQuery(id+"F0.wireOp",EDGE,"E0.right")])]}),"instanceName":"1"});
            var Q58;
            Q58=makeQuery(id+"F2.opExtrude","SWEPT_BODY",BODY,{"disambiguationData":[OSD([sQuery(id+"F0.wireOp",EDGE,"E0.right")])]});
            var Q59;
            Q59=makeQuery(id+"F25.opPattern","COPY",BODY,{"derivedFrom":makeQuery(id+"F24.opPattern","COPY",BODY,{"derivedFrom":makeQuery(id+"F2.opExtrude","SWEPT_BODY",BODY,{"disambiguationData":[OSD([sQuery(id+"F0.wireOp",EDGE,"E0.right")])]}),"instanceName":"1"}),"instanceName":"1"});
            var Q60;
            Q60=makeQuery(id+"F26.opPattern","COPY",BODY,{"derivedFrom":makeQuery(id+"F25.opPattern","COPY",BODY,{"derivedFrom":makeQuery(id+"F24.opPattern","COPY",BODY,{"derivedFrom":makeQuery(id+"F2.opExtrude","SWEPT_BODY",BODY,{"disambiguationData":[OSD([sQuery(id+"F0.wireOp",EDGE,"E0.right")])]}),"instanceName":"1"}),"instanceName":"1"}),"instanceName":"1"});
            var Q61;
            Q61=makeQuery(id+"F27.opPattern","COPY",BODY,{"derivedFrom":makeQuery(id+"F23.opPattern","COPY",BODY,{"derivedFrom":makeQuery(id+"F22.opPattern","COPY",BODY,{"derivedFrom":makeQuery(id+"F18.opExtrude","SWEPT_BODY",BODY,{"disambiguationData":[OSD([sQuery(id+"F0.wireOp",EDGE,"E0.top")])]}),"instanceName":"1"}),"instanceName":"1"}),"instanceName":"1"});
            var Q62;
            Q62=makeQuery(id+"F23.opPattern","COPY",BODY,{"derivedFrom":makeQuery(id+"F22.opPattern","COPY",BODY,{"derivedFrom":makeQuery(id+"F18.opExtrude","SWEPT_BODY",BODY,{"disambiguationData":[OSD([sQuery(id+"F0.wireOp",EDGE,"E0.top")])]}),"instanceName":"1"}),"instanceName":"1"});
            var Q63;
            Q63=makeQuery(id+"F22.opPattern","COPY",BODY,{"derivedFrom":makeQuery(id+"F18.opExtrude","SWEPT_BODY",BODY,{"disambiguationData":[OSD([sQuery(id+"F0.wireOp",EDGE,"E0.top")])]}),"instanceName":"1"});
            var Q64;
            Q64=makeQuery(id+"F22.opPattern","COPY",BODY,{"derivedFrom":makeQuery(id+"F14.opExtrude","SWEPT_BODY",BODY,{"disambiguationData":[OSD([sQuery(id+"F0.wireOp",EDGE,"E0.top")])]}),"instanceName":"1"});
            var Q65;
            Q65=makeQuery(id+"F22.opPattern","COPY",BODY,{"derivedFrom":makeQuery(id+"F12.opExtrude","SWEPT_BODY",BODY,{"disambiguationData":[OSD([sQuery(id+"F0.wireOp",EDGE,"E0.top")])]}),"instanceName":"1"});
            var Q66;
            Q66=makeQuery(id+"F7.opExtrude","SWEPT_BODY",BODY,{"disambiguationData":[OSD([sQuery(id+"F0.wireOp",EDGE,"E0.top"),sQuery(id+"F0.wireOp",EDGE,"E0.right")])]});
            var Q67;
            Q67=makeQuery(id+"F22.opPattern","COPY",BODY,{"derivedFrom":makeQuery(id+"F16.opExtrude","SWEPT_BODY",BODY,{"disambiguationData":[OSD([sQuery(id+"F0.wireOp",EDGE,"E0.top")])]}),"instanceName":"1"});
            transform(context, id + "F28", {"entities" : qUnion([Q0, Q1, Q2, Q3, Q4, Q5, Q6, Q7, Q8, Q9, Q10, Q11, Q12, Q13, Q14, Q15, Q16, Q17, Q18, Q19, Q20, Q21, Q22, Q23, Q24, Q25, Q26, Q27, Q28, Q29, Q30, Q31, Q32, Q33, Q34, Q35, Q36, Q37, Q38, Q39, Q40, Q41, Q42, Q43, Q44, Q45, Q46, Q47, Q48, Q49, Q50, Q51, Q52, Q53, Q54, Q55, Q56, Q57, Q58, Q59, Q60, Q61, Q62, Q63, Q64, Q65, Q66, Q67]), "transformType" : TransformType.TRANSLATION_3D, "dx" : 1632 * mm, "dy" : 0 * mm, "dz" : 0 * mm, "makeCopy" : true});
        }
    });
